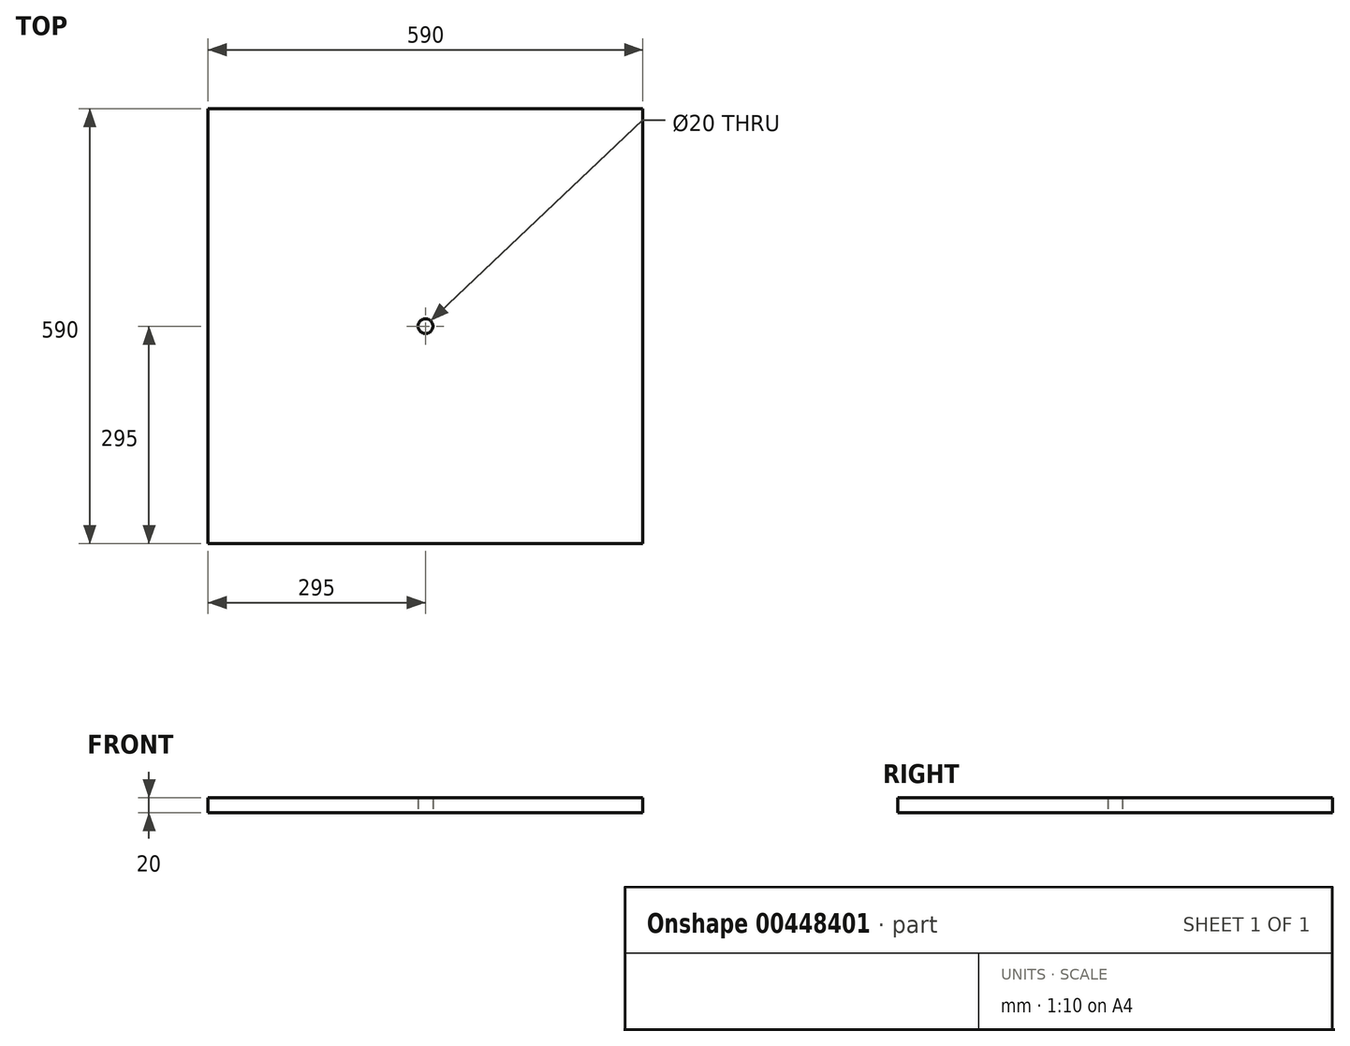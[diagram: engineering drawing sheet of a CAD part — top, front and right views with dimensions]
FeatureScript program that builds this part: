
annotation { "Feature Type Name" : "Feature", "Feature Type Description" : "" }
export const myFeature = defineFeature(function(context is Context, id is Id, definition is map)
    precondition{}
    {
        {
            var Q0;
            Q0=qCreatedBy(makeId("Top.planeOp"),FACE);
            var sketch = newSketch(context, id + "F0", { "sketchPlane" : qUnion([Q0])});
            skLineSegment(sketch, "E0.bottom", {"start": v(295, -295) * mm, "end": v(-295, -295) * mm});
            skLineSegment(sketch, "E0.top", {"start": v(295, 295) * mm, "end": v(-295, 295) * mm});
            skLineSegment(sketch, "E0.left", {"start": v(295, -295) * mm, "end": v(295, 295) * mm});
            skLineSegment(sketch, "E0.right", {"start": v(-295, -295) * mm, "end": v(-295, 295) * mm});
            skPoint(sketch, "E0.middle", {"position": v(0, 0) * mm});
            skCircle(sketch, "E1", {"center": v(0, 0) * mm, "radius": 10 * mm});
            skSolve(sketch);
        }
        {
            var Q0;
            Q0=makeQuery(id+"F0.imprint","IMPRINT",FACE,{"disambiguationData":[TD([[makeQuery(id+"F0.imprint","IMPRINT",EDGE,{"derivedFrom":sQuery(id+"F0.wireOp",EDGE,"E0.bottom")}),-1.0]])]});
            extrude(context, id + "F1", {"entities" : qUnion([Q0]), "depth" : 20 * mm});
        }
    });
